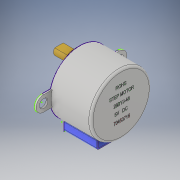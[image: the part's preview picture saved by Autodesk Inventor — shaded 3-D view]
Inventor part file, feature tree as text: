
AUTODESK INVENTOR PART (.ipt)
format: ipt  version: 2017 (Build 210142000, 142)  size: 556,544 bytes
history: native  units: in
note: dims shown in document units (in); Inventor stores cm internally (conversion verified against a paired STEP export)
features: other x2, sketch x1
ambient origin geometry x8: Origin, YZ Plane, XZ Plane, XY Plane, X Axis, Y Axis, Z Axis, Center Point
bodies: Solid1 (feature_tree), Solid2 (feature_tree)
feature tree (3):
  sketch  "Sketch4"
  other  "Split3[1]"
  other  "Split3[2]"
